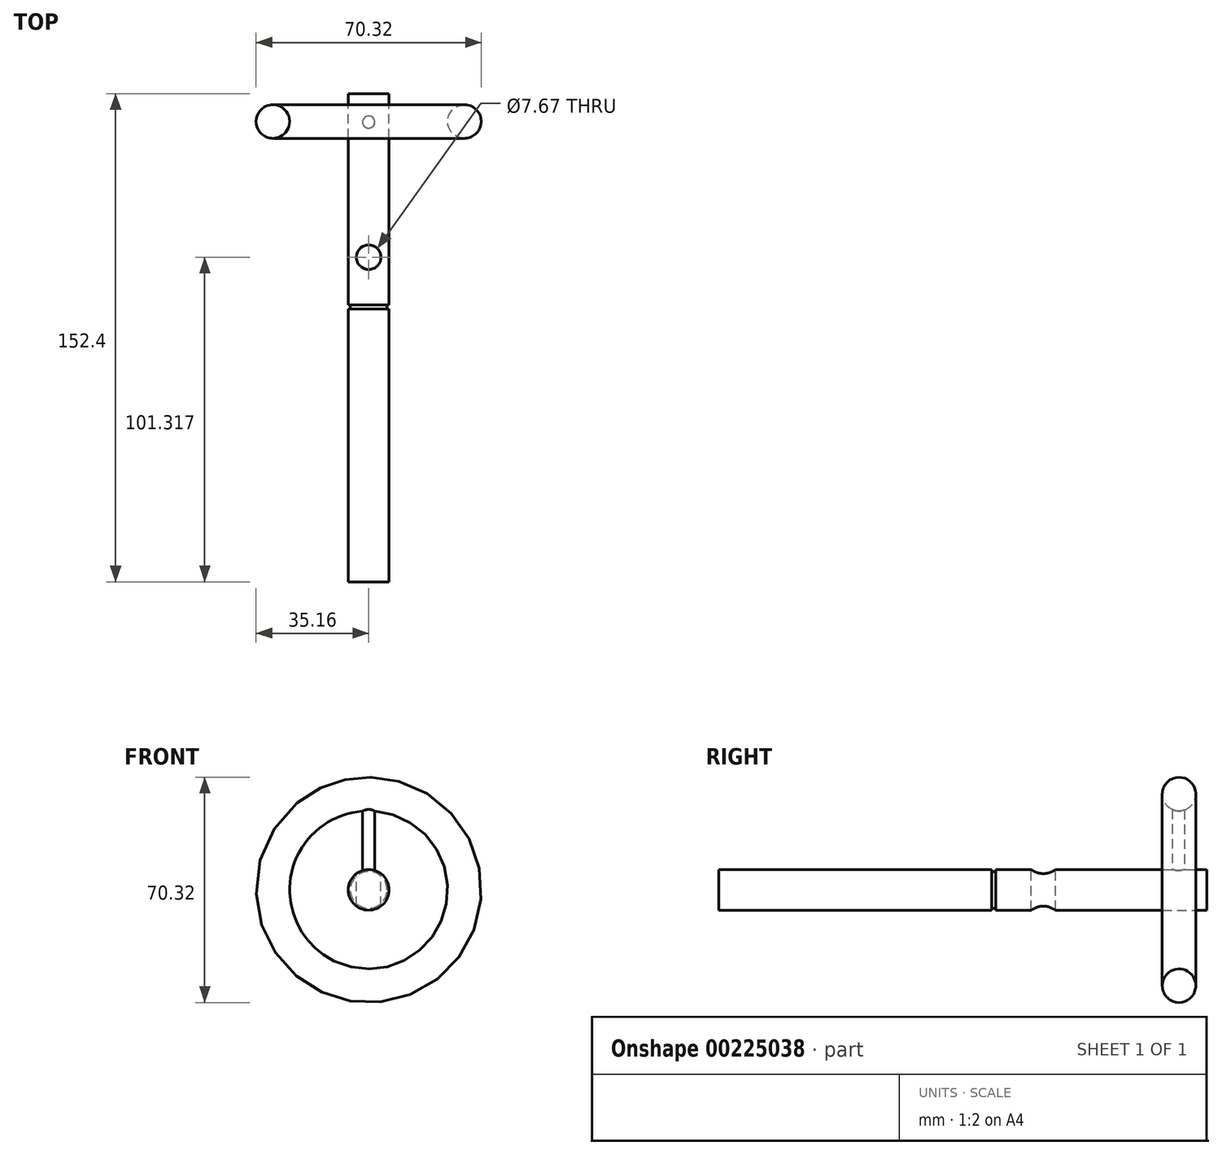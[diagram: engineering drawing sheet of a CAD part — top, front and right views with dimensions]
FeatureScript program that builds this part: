
annotation { "Feature Type Name" : "Feature", "Feature Type Description" : "" }
export const myFeature = defineFeature(function(context is Context, id is Id, definition is map)
    precondition{}
    {
        {
            var Q0;
            Q0=qCreatedBy(makeId("Front.planeOp"),FACE);
            var sketch = newSketch(context, id + "F0", { "sketchPlane" : qUnion([Q0])});
            skCircle(sketch, "E0", {"center": v(0, 0) * mm, "radius": 6.35 * mm});
            skSolve(sketch);
        }
        {
            var Q0;
            Q0 = qSketchRegion(id + "F0", true);
            extrude(context, id + "F1", {"entities" : qUnion([Q0]), "depth" : 152.4 * mm});
        }
        {
            var Q0;
            Q0=makeQuery(id+"F1.opExtrude","CAP_FACE",FACE,{"disambiguationData":[OSD([sQuery(id+"F0.wireOp",EDGE,"E0")])],"isStart":false});
            cPlane(context, id + "F2", {"entities" : qUnion([Q0]), "cplaneType" : CPlaneType.OFFSET, "offset" : 85.22 * mm, "oppositeDirection" : true, "width" : 152.4 * mm, "height" : 152.4 * mm});
        }
        {
            var Q0;
            Q0=qCreatedBy(id+"F2.planeOp",FACE);
            var sketch = newSketch(context, id + "F3", { "sketchPlane" : qUnion([Q0])});
            skCircle(sketch, "E1", {"center": v(0, 0) * mm, "radius": 6.35 * mm});
            skCircle(sketch, "E2", {"center": v(0, 0) * mm, "radius": 5.72 * mm});
            skSolve(sketch);
        }
        {
            var Q0;
            Q0 = qSketchRegion(id + "F3", true);
            extrude(context, id + "F4", {"entities" : qUnion([Q0]), "operationType" : NewBodyOperationType.REMOVE, "oppositeDirection" : true, "depth" : 1.27 * mm});
        }
        {
            var Q0;
            Q0=qCreatedBy(makeId("Top.planeOp"),FACE);
            var sketch = newSketch(context, id + "F5", { "sketchPlane" : qUnion([Q0])});
            skCircle(sketch, "E3", {"center": v(0, -51.08) * mm, "radius": 3.84 * mm});
            skSolve(sketch);
        }
        {
            var Q0;
            Q0 = qSketchRegion(id + "F5", true);
            extrude(context, id + "F6", {"entities" : qUnion([Q0]), "operationType" : NewBodyOperationType.REMOVE, "oppositeDirection" : true, "depth" : 25.4 * mm, "symmetric" : true});
        }
        {
            var Q0;
            Q0=qCreatedBy(makeId("Top.planeOp"),FACE);
            var sketch = newSketch(context, id + "F7", { "sketchPlane" : qUnion([Q0])});
            skCircle(sketch, "E4", {"center": v(0, -8.9) * mm, "radius": 1.9 * mm});
            skSolve(sketch);
        }
        {
            var Q0;
            Q0 = qSketchRegion(id + "F7", true);
            extrude(context, id + "F8", {"entities" : qUnion([Q0]), "operationType" : NewBodyOperationType.ADD, "depth" : 25.4 * mm});
        }
        {
            var Q0;
            Q0=qCreatedBy(makeId("Right.planeOp"),FACE);
            var sketch = newSketch(context, id + "F9", { "sketchPlane" : qUnion([Q0])});
            skLineSegment(sketch, "E5", {"start": v(-157.88, 0) * mm, "end": v(12.94, 0) * mm, "construction": true});
            skSolve(sketch);
        }
        {
            var Q0;
            Q0=qCreatedBy(makeId("Front.planeOp"),FACE);
            cPlane(context, id + "F10", {"entities" : qUnion([Q0]), "cplaneType" : CPlaneType.OFFSET, "offset" : 8.9 * mm, "width" : 152.4 * mm, "height" : 152.4 * mm});
        }
        {
            var Q0;
            Q0=qCreatedBy(makeId("Top.planeOp"),FACE);
            var sketch = newSketch(context, id + "F11", { "sketchPlane" : qUnion([Q0])});
            skCircle(sketch, "E6", {"center": v(-29.92, -8.71) * mm, "radius": 5.24 * mm});
            skSolve(sketch);
        }
        {
            var Q0;
            Q0 = qSketchRegion(id + "F11", true);
            var Q1;
            Q1=sQuery(id+"F9.wireOp",EDGE,"E5");
            revolve(context, id + "F12", {"operationType" : NewBodyOperationType.ADD, "entities" : qUnion([Q0]), "axis" : qUnion([Q1]), "revolveType" : RevolveType.FULL});
        }
    });
